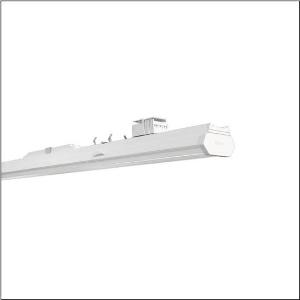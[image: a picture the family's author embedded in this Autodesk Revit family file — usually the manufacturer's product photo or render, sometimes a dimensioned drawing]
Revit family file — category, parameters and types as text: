
# Revit family: licross_r__11_protected_extreme_mo_51td1bdn49xge_f438
name_source: partatom
category: Lighting Fixtures
units: mm (PartAtom-declared; Revit-internal decimal feet)

## family parameters
Cut with Voids When Loaded = No
Host = Face
Light Source = No
Part Type = Normal
Room Calculation Point = No
Round Connector Dimension = Use Diameter
Shared = No

## types (1)
- --- (1 x LED, 9370 lm, 57.1 W, 4000K)
    Apparent Load = 57 VA
    CIE Flux Codes = 54 82 95 97 100
    Color Rendering = 80
    Color Temperature = 4000K
    Default Elevation = 1800 mm
    Description = Licross® 11 Protected extreme MO, luminaire insert, of sheet steel, galvanised, coil coated, white, length: 1.500mm, width: 90mm, height: 101mm, LED rated luminous flux: 9.370lm, light colour: 840, control gear: DALI 2, with plug, 5-pole, with phase selection, mains connection: 220..240V, AC, 50/60Hz, rated input power: 57W, halogen-free wiring, primary optical cover: cover, of PMMA, light emission: direct distribution, primary light characteristic: symmetric, protection rating (complete): IP54, insulation class (complete): insulation class I (protective earthing), certification: CE, ENEC, VDE, UKCA, protection symbol: D if used in an environment with non-conductive dust loads with corresponding accessories, impact resistance: IK06, permissible ambient temperature for indoor applications: -40..+35°C, corresponds to IFS (International Featured Standards) requirements for safety and quality in the food industry, reducing of maximum allowable ambient temperature of 5°C with ceiling mounting, LABS conformity tested according to VDMA 24364:2018-05, packaging unit: 1 piece
    Height = 92 mm
    Lamp = 1 x LED
    Lamp Light Flux = 9370 lm
    Lamp Power = 57.1 W
    Lamp count = 1
    Length = 1500 mm
    Luminous efficacy = 164 lm/W
    Manufacturer = Siteco
    ModVariant = No
    Model = 51TD1BDN49XGE
    Mounting Place = Ceiling
    Mounting Type = Pendant
    Number of Poles = 1
    OnlyDefault = Yes
    Power Factor = 1
    Product Name = Licross® 11 Protected extreme MO
    Product group = luminaire insert
    ProductGroupID = 901
    Protection Class = Protection class I
    Protection Degree = IP 54
    RLX_Detail_Level = 1
    RLX_Emergency_Light_Flux = 0 lm
    RLX_Emergency_Type = 0
    RLX_Emergency_Type_DB = No
    RlxData = <blob elided: 24337 chars, md5=593da9e4>
    Socket = socket
    Standby Power = 0 W
    System Light Flux = 9370 lm
    System Power = 57 W
    Type Comments = factory setting: luminous flux: 100 % | dim-lin: 254 | 378 mA
    Type Image = l_1256145.jpg
    URL = http://relux.com
    VarID = @adj_077868
    Voltage = 0 V
    Weight = 0.00 kg
    Width = 88 mm

## geometry (parser evidence)
native form markers: Blend x4, Sweep x10
no freeform markers — native parametric forms only
